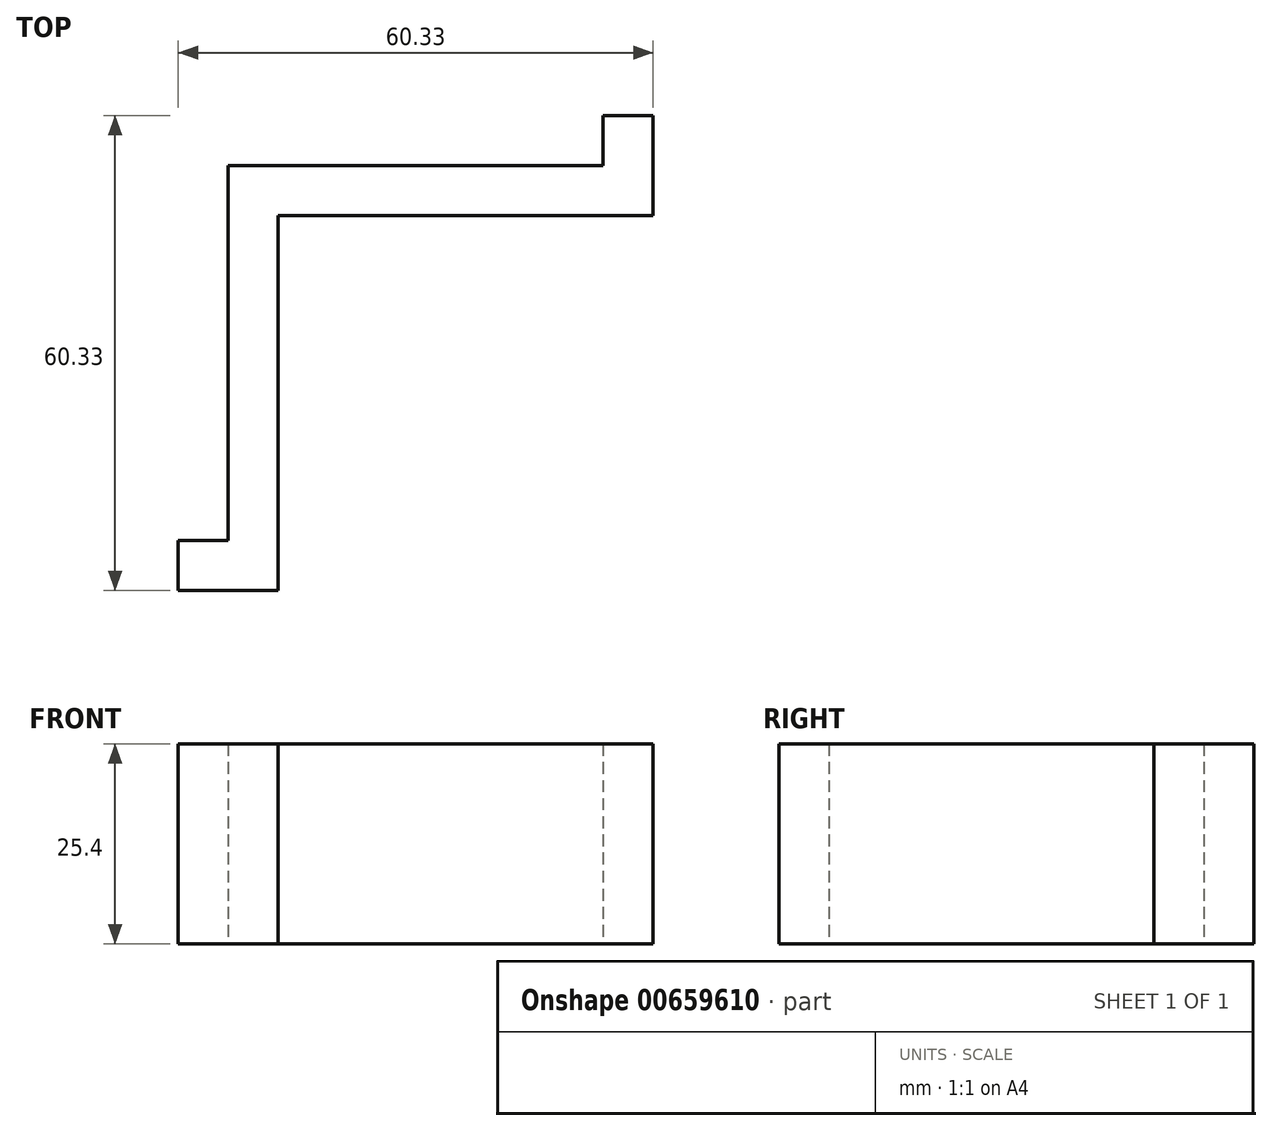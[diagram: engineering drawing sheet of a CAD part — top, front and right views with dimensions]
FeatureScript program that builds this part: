
annotation { "Feature Type Name" : "Feature", "Feature Type Description" : "" }
export const myFeature = defineFeature(function(context is Context, id is Id, definition is map)
    precondition{}
    {
        {
            var Q0;
            Q0=qCreatedBy(makeId("Top.planeOp"),FACE);
            var sketch = newSketch(context, id + "F0", { "sketchPlane" : qUnion([Q0])});
            skLineSegment(sketch, "E0.bottom", {"start": v(25.4, -25.4) * mm, "end": v(-25.4, -25.4) * mm});
            skLineSegment(sketch, "E0.top", {"start": v(25.4, 25.4) * mm, "end": v(-25.4, 25.4) * mm});
            skLineSegment(sketch, "E0.left", {"start": v(25.4, -25.4) * mm, "end": v(25.4, 25.4) * mm});
            skLineSegment(sketch, "E0.right", {"start": v(-25.4, -25.4) * mm, "end": v(-25.4, 25.4) * mm});
            skPoint(sketch, "E0.middle", {"position": v(0, 0) * mm});
            skLineSegment(sketch, "E1", {"start": v(22.23, 25.4) * mm, "end": v(22.23, 31.75) * mm});
            skLineSegment(sketch, "E2", {"start": v(22.23, 31.75) * mm, "end": v(-31.75, 31.75) * mm});
            skLineSegment(sketch, "E3", {"start": v(-31.75, 31.75) * mm, "end": v(-31.75, -22.23) * mm});
            skLineSegment(sketch, "E4", {"start": v(-31.75, -22.23) * mm, "end": v(-25.4, -22.23) * mm});
            skSolve(sketch);
        }
        {
            var Q0;
            {var subQ0=sQuery(id+"F0.wireOp",EDGE,"E1");Q0=makeQuery(id+"F0.imprint","IMPRINT",FACE,{"disambiguationData":[TD([[makeQuery(id+"F0.imprint","IMPRINT",EDGE,{"derivedFrom":subQ0}),1.0]])]});}
            extrude(context, id + "F1", {"entities" : qUnion([Q0]), "depth" : 25.4 * mm, "offsetDistance" : 25.4 * mm});
        }
        {
            var Q0;
            Q0=makeQuery(id+"F1.opExtrude","SWEPT_FACE",FACE,{"disambiguationData":[OSD([sQuery(id+"F0.wireOp",EDGE,"E3")])]});
            var sketch = newSketch(context, id + "F2", { "sketchPlane" : qUnion([Q0])});
            skLineSegment(sketch, "E5", {"start": v(15.87, 25.4) * mm, "end": v(15.87, 0) * mm});
            skSolve(sketch);
        }
        {
            var Q0;
            Q0=makeQuery(id+"F1.opExtrude","SWEPT_FACE",FACE,{"disambiguationData":[OSD([sQuery(id+"F0.wireOp",EDGE,"E2")])]});
            var sketch = newSketch(context, id + "F3", { "sketchPlane" : qUnion([Q0])});
            skLineSegment(sketch, "E6", {"start": v(-15.88, 25.4) * mm, "end": v(-15.88, 0) * mm});
            skSolve(sketch);
        }
        {
            var Q0;
            {var subQ0=sQuery(id+"F3.wireOp",EDGE,"E6");Q0=makeQuery(id+"F3.imprint","IMPRINT",FACE,{"disambiguationData":[TD([[makeQuery(id+"F3.imprint","IMPRINT",EDGE,{"derivedFrom":subQ0}),-1.0]])]});}
            extrude(context, id + "F4", {"entities" : qUnion([Q0]), "operationType" : NewBodyOperationType.ADD, "depth" : 6.35 * mm, "offsetDistance" : 25.4 * mm});
        }
        {
            var Q0;
            {var subQ0=sQuery(id+"F2.wireOp",EDGE,"E5");Q0=makeQuery(id+"F2.imprint","IMPRINT",FACE,{"disambiguationData":[TD([[makeQuery(id+"F2.imprint","IMPRINT",EDGE,{"derivedFrom":subQ0}),1.0]])]});}
            extrude(context, id + "F5", {"entities" : qUnion([Q0]), "operationType" : NewBodyOperationType.ADD, "depth" : 6.35 * mm, "offsetDistance" : 25.4 * mm});
        }
    });
